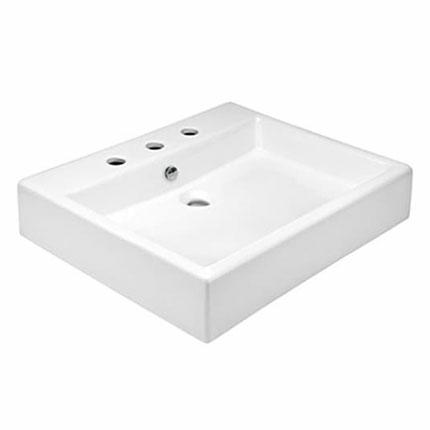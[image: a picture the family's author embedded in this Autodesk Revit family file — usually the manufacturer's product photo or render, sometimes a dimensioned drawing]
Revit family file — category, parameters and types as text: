
# Revit family: LV LUCERNA3_RFA
name_source: partatom
category: Aparatos sanitarios
revit_build: Autodesk Revit 2016 (Build: 20150220_1215(x64)
units: mm (PartAtom-declared; Revit-internal decimal feet)

## family parameters
Compartido = No
Corte con vacíos al cargar = No
Cota de conector redondo = Diámetro de uso
Número OmniClass = 23.45.00.00
Punto de cálculo de habitación = No
Se basa en plano de trabajo = No
Siempre vertical = Sí
Tipo de pieza = Normal
Título OmniClass = Sanitary, Laundry, and Cleaning Equipment

## types (1)
- LV LUCERNA3
    Comentarios de tipo = SANIVEX
    Data Sheet = https://www.helvex.com.mx
    Descripción = LAVABO LUCERNA TRES PERFORACIONES DE SOBREPONER CON REBOSADERO
    Fabricante = HELVEX
    Features = Perfect Assembly; Uniformity
    High Gloss Ceramic = High Gloss Ceramic
    Imagen de tipo = LV LUCERNA3.jpg
    Instructive = https://www.helvex.com.mx
    Modelo = LV LUCERNA3
    Total Height = 5"
    Total Length = 18"
    Total Width = 22"
    URL = https://www.helvex.com.mx

## geometry (parser evidence)
native form markers: Sweep x3
no freeform markers — native parametric forms only
